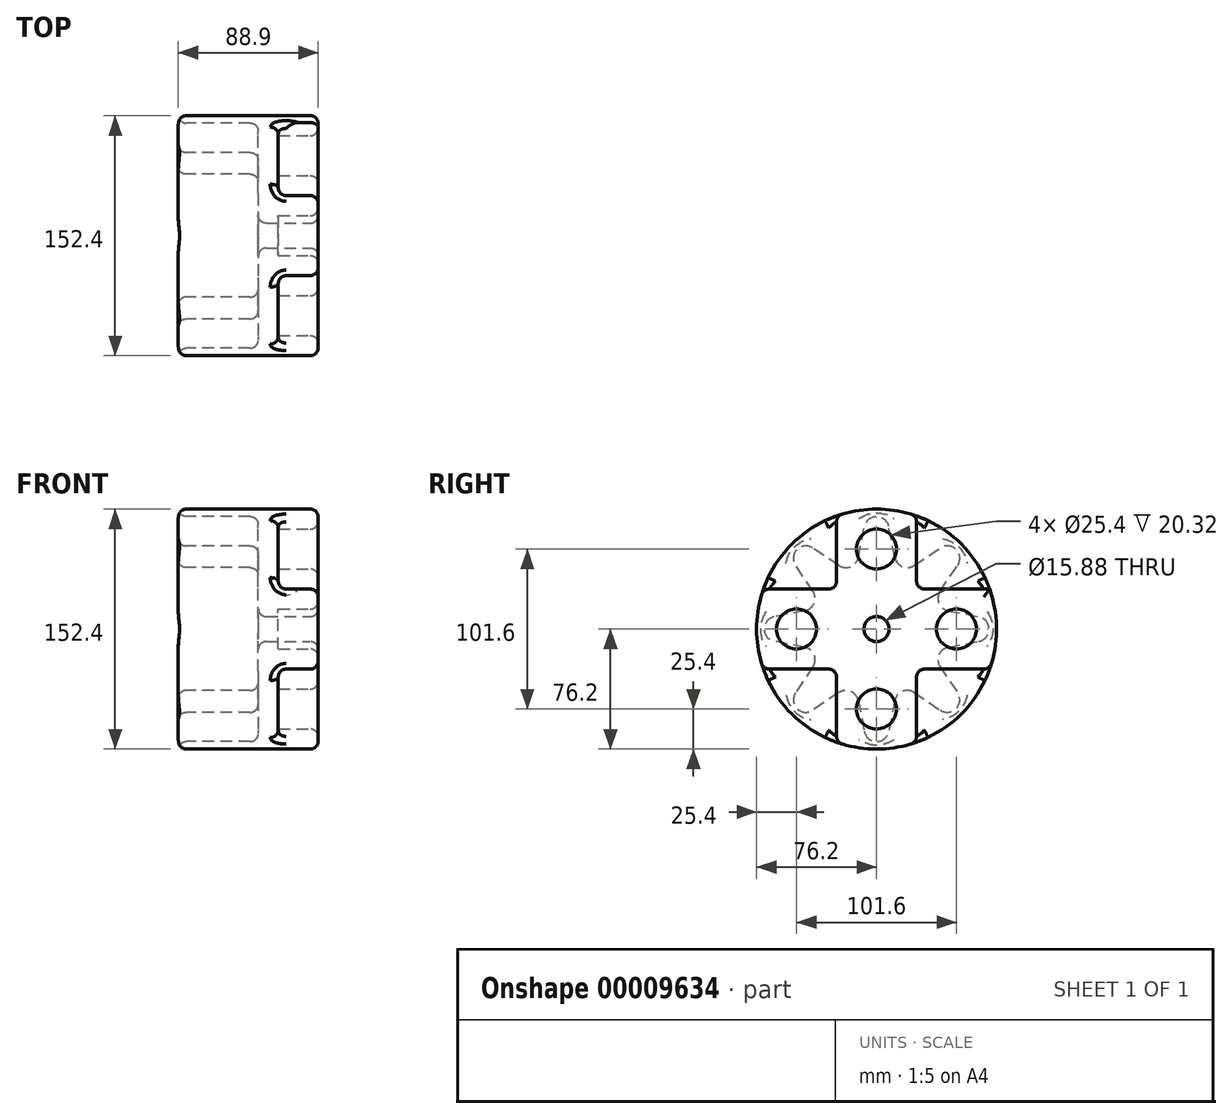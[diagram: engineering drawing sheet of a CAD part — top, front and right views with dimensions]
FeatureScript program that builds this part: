
annotation { "Feature Type Name" : "Feature", "Feature Type Description" : "" }
export const myFeature = defineFeature(function(context is Context, id is Id, definition is map)
    precondition{}
    {
        {
            var Q0;
            Q0=qCreatedBy(makeId("Right.planeOp"),FACE);
            var sketch = newSketch(context, id + "F0", { "sketchPlane" : qUnion([Q0])});
            skCircle(sketch, "E0", {"center": v(0, 0) * mm, "radius": 76.2 * mm});
            skSolve(sketch);
        }
        {
            var Q0;
            Q0 = qSketchRegion(id + "F0", true);
            extrude(context, id + "F1", {"entities" : qUnion([Q0]), "depth" : 88.9 * mm});
        }
        {
            var Q0;
            Q0=makeQuery(id+"F1.opExtrude","CAP_FACE",FACE,{"disambiguationData":[OSD([sQuery(id+"F0.wireOp",EDGE,"E0")])],"isStart":true});
            var sketch = newSketch(context, id + "F2", { "sketchPlane" : qUnion([Q0])});
            skArc(sketch, "E1", {"start": v(7.79, 65.03) * mm, "mid": v(0, 71.44) * mm, "end": v(-7.79, 65.03) * mm});
            skArc(sketch, "E2", {"start": v(-16.4, 39.6) * mm, "mid": v(-13.3, 41.9) * mm, "end": v(-11.65, 45.4) * mm});
            skLineSegment(sketch, "E3", {"start": v(-19.44, 46.93) * mm, "end": v(0, 0) * mm, "construction": true});
            skLineSegment(sketch, "E4", {"start": v(0, 0) * mm, "end": v(0, 63.5) * mm, "construction": true});
            skLineSegment(sketch, "E5", {"start": v(-11.65, 45.4) * mm, "end": v(-7.79, 65.03) * mm});
            skLineSegment(sketch, "E6.0.MirrorCS", {"start": v(11.65, 45.4) * mm, "end": v(7.79, 65.03) * mm});
            skArc(sketch, "E7.0.MirrorCS", {"start": v(-16.4, 39.6) * mm, "mid": v(-20.23, 39.03) * mm, "end": v(-23.86, 40.34) * mm});
            skArc(sketch, "E8.1.0", {"start": v(-39.6, 16.4) * mm, "mid": v(-41.9, 13.3) * mm, "end": v(-45.4, 11.65) * mm});
            skArc(sketch, "E8.1.1", {"start": v(-39.6, 16.4) * mm, "mid": v(-39.03, 20.23) * mm, "end": v(-40.34, 23.86) * mm});
            skLineSegment(sketch, "E8.1.2", {"start": v(-40.34, 23.86) * mm, "end": v(-51.5, 40.48) * mm});
            skArc(sketch, "E8.1.3", {"start": v(-40.48, 51.5) * mm, "mid": v(-50.51, 50.51) * mm, "end": v(-51.5, 40.48) * mm});
            skLineSegment(sketch, "E8.1.4", {"start": v(-23.86, 40.34) * mm, "end": v(-40.48, 51.5) * mm});
            skArc(sketch, "E8.2.0", {"start": v(-39.6, -16.4) * mm, "mid": v(-39.03, -20.23) * mm, "end": v(-40.34, -23.86) * mm});
            skArc(sketch, "E8.2.1", {"start": v(-39.6, -16.4) * mm, "mid": v(-41.9, -13.3) * mm, "end": v(-45.4, -11.65) * mm});
            skLineSegment(sketch, "E8.2.2", {"start": v(-45.4, -11.65) * mm, "end": v(-65.03, -7.79) * mm});
            skArc(sketch, "E8.2.3", {"start": v(-65.03, 7.79) * mm, "mid": v(-71.44, 0) * mm, "end": v(-65.03, -7.79) * mm});
            skLineSegment(sketch, "E8.2.4", {"start": v(-45.4, 11.65) * mm, "end": v(-65.03, 7.79) * mm});
            skArc(sketch, "E8.3.0", {"start": v(-16.4, -39.6) * mm, "mid": v(-13.3, -41.9) * mm, "end": v(-11.65, -45.4) * mm});
            skArc(sketch, "E8.3.1", {"start": v(-16.4, -39.6) * mm, "mid": v(-20.23, -39.03) * mm, "end": v(-23.86, -40.34) * mm});
            skLineSegment(sketch, "E8.3.2", {"start": v(-23.86, -40.34) * mm, "end": v(-40.48, -51.5) * mm});
            skArc(sketch, "E8.3.3", {"start": v(-51.5, -40.48) * mm, "mid": v(-50.51, -50.51) * mm, "end": v(-40.48, -51.5) * mm});
            skLineSegment(sketch, "E8.3.4", {"start": v(-40.34, -23.86) * mm, "end": v(-51.5, -40.48) * mm});
            skArc(sketch, "E8.4.0", {"start": v(16.4, -39.6) * mm, "mid": v(20.23, -39.03) * mm, "end": v(23.86, -40.34) * mm});
            skArc(sketch, "E8.4.1", {"start": v(16.4, -39.6) * mm, "mid": v(13.3, -41.9) * mm, "end": v(11.65, -45.4) * mm});
            skLineSegment(sketch, "E8.4.2", {"start": v(11.65, -45.4) * mm, "end": v(7.79, -65.03) * mm});
            skArc(sketch, "E8.4.3", {"start": v(-7.79, -65.03) * mm, "mid": v(0, -71.44) * mm, "end": v(7.79, -65.03) * mm});
            skLineSegment(sketch, "E8.4.4", {"start": v(-11.65, -45.4) * mm, "end": v(-7.79, -65.03) * mm});
            skArc(sketch, "E8.5.0", {"start": v(39.6, -16.4) * mm, "mid": v(41.9, -13.3) * mm, "end": v(45.4, -11.65) * mm});
            skArc(sketch, "E8.5.1", {"start": v(39.6, -16.4) * mm, "mid": v(39.03, -20.23) * mm, "end": v(40.34, -23.86) * mm});
            skLineSegment(sketch, "E8.5.2", {"start": v(40.34, -23.86) * mm, "end": v(51.5, -40.48) * mm});
            skArc(sketch, "E8.5.3", {"start": v(40.48, -51.5) * mm, "mid": v(50.51, -50.51) * mm, "end": v(51.5, -40.48) * mm});
            skLineSegment(sketch, "E8.5.4", {"start": v(23.86, -40.34) * mm, "end": v(40.48, -51.5) * mm});
            skArc(sketch, "E8.6.0", {"start": v(39.6, 16.4) * mm, "mid": v(39.03, 20.23) * mm, "end": v(40.34, 23.86) * mm});
            skArc(sketch, "E8.6.1", {"start": v(39.6, 16.4) * mm, "mid": v(41.9, 13.3) * mm, "end": v(45.4, 11.65) * mm});
            skLineSegment(sketch, "E8.6.2", {"start": v(45.4, 11.65) * mm, "end": v(65.03, 7.79) * mm});
            skArc(sketch, "E8.6.3", {"start": v(65.03, -7.79) * mm, "mid": v(71.44, 0) * mm, "end": v(65.03, 7.79) * mm});
            skLineSegment(sketch, "E8.6.4", {"start": v(45.4, -11.65) * mm, "end": v(65.03, -7.79) * mm});
            skArc(sketch, "E8.7.0", {"start": v(16.4, 39.6) * mm, "mid": v(13.3, 41.9) * mm, "end": v(11.65, 45.4) * mm});
            skArc(sketch, "E8.7.1", {"start": v(16.4, 39.6) * mm, "mid": v(20.23, 39.03) * mm, "end": v(23.86, 40.34) * mm});
            skLineSegment(sketch, "E8.7.2", {"start": v(23.86, 40.34) * mm, "end": v(40.48, 51.5) * mm});
            skArc(sketch, "E8.7.3", {"start": v(51.5, 40.48) * mm, "mid": v(50.51, 50.51) * mm, "end": v(40.48, 51.5) * mm});
            skLineSegment(sketch, "E8.7.4", {"start": v(40.34, 23.86) * mm, "end": v(51.5, 40.48) * mm});
            skPoint(sketch, "E8.center", {"position": v(0, 0) * mm});
            skSolve(sketch);
        }
        {
            var Q0;
            Q0=makeQuery(id+"F2.imprint","IMPRINT",FACE,{"disambiguationData":[TD([[makeQuery(id+"F2.imprint","IMPRINT",EDGE,{"derivedFrom":sQuery(id+"F2.wireOp",EDGE,"E1")}),1.0]])]});
            var Q1;
            Q1=makeQuery(id+"F1.opExtrude","CAP_FACE",FACE,{"disambiguationData":[OSD([sQuery(id+"F0.wireOp",EDGE,"E0")])],"isStart":false});
            extrude(context, id + "F3", {"entities" : qUnion([Q0]), "operationType" : NewBodyOperationType.REMOVE, "oppositeDirection" : true, "endBoundEntity" : qUnion([Q1]), "depth" : 50.8 * mm});
        }
        {
            var Q0;
            Q0=makeQuery(id+"F1.opExtrude","CAP_FACE",FACE,{"disambiguationData":[OSD([sQuery(id+"F0.wireOp",EDGE,"E0")])],"isStart":false});
            var sketch = newSketch(context, id + "F4", { "sketchPlane" : qUnion([Q0])});
            skCircle(sketch, "E9", {"center": v(0, 50.8) * mm, "radius": 12.7 * mm});
            skCircle(sketch, "E10.1.0", {"center": v(-50.8, 0) * mm, "radius": 12.7 * mm});
            skCircle(sketch, "E10.2.0", {"center": v(0, -50.8) * mm, "radius": 12.7 * mm});
            skCircle(sketch, "E10.3.0", {"center": v(50.8, 0) * mm, "radius": 12.7 * mm});
            skPoint(sketch, "E10.center", {"position": v(0, 0) * mm});
            skLineSegment(sketch, "E11", {"start": v(-50.8, 0) * mm, "end": v(0, 50.8) * mm, "construction": true});
            skLineSegment(sketch, "E12", {"start": v(0, 0) * mm, "end": v(0, 76.2) * mm, "construction": true});
            skLineSegment(sketch, "E13", {"start": v(0, 0) * mm, "end": v(-50.8, 0) * mm, "construction": true});
            skSolve(sketch);
        }
        {
            var Q0;
            Q0 = qSketchRegion(id + "F4", true);
            extrude(context, id + "F5", {"entities" : qUnion([Q0]), "operationType" : NewBodyOperationType.REMOVE, "oppositeDirection" : true, "depth" : 25.4 * mm});
        }
        {
            var Q0;
            Q0=makeQuery(id+"F1.opExtrude","CAP_FACE",FACE,{"disambiguationData":[OSD([sQuery(id+"F0.wireOp",EDGE,"E0")])],"isStart":false});
            var sketch = newSketch(context, id + "F6", { "sketchPlane" : qUnion([Q0])});
            skLineSegment(sketch, "E14.top", {"start": v(-71.84, 25.4) * mm, "end": v(-25.4, 25.4) * mm});
            skLineSegment(sketch, "E14.right", {"start": v(-25.4, 71.84) * mm, "end": v(-25.4, 25.4) * mm});
            skLineSegment(sketch, "E15", {"start": v(0, 63.5) * mm, "end": v(0, 76.2) * mm, "construction": true});
            skLineSegment(sketch, "E16", {"start": v(-12.7, 50.8) * mm, "end": v(-25.4, 50.8) * mm, "construction": true});
            skCircle(sketch, "E17.0", {"center": v(0, 50.8) * mm, "radius": 12.7 * mm, "construction": true});
            skArc(sketch, "E18.0", {"start": v(-25.4, 71.84) * mm, "mid": v(-53.88, 53.88) * mm, "end": v(-71.84, 25.4) * mm});
            skLineSegment(sketch, "E19.1.0", {"start": v(-71.84, -25.4) * mm, "end": v(-25.4, -25.4) * mm});
            skArc(sketch, "E19.1.1", {"start": v(-71.84, -25.4) * mm, "mid": v(-53.88, -53.88) * mm, "end": v(-25.4, -71.84) * mm});
            skLineSegment(sketch, "E19.1.2", {"start": v(-25.4, -71.84) * mm, "end": v(-25.4, -25.4) * mm});
            skLineSegment(sketch, "E19.2.0", {"start": v(25.4, -71.84) * mm, "end": v(25.4, -25.4) * mm});
            skArc(sketch, "E19.2.1", {"start": v(25.4, -71.84) * mm, "mid": v(53.88, -53.88) * mm, "end": v(71.84, -25.4) * mm});
            skLineSegment(sketch, "E19.2.2", {"start": v(71.84, -25.4) * mm, "end": v(25.4, -25.4) * mm});
            skLineSegment(sketch, "E19.3.0", {"start": v(71.84, 25.4) * mm, "end": v(25.4, 25.4) * mm});
            skArc(sketch, "E19.3.1", {"start": v(71.84, 25.4) * mm, "mid": v(53.88, 53.88) * mm, "end": v(25.4, 71.84) * mm});
            skLineSegment(sketch, "E19.3.2", {"start": v(25.4, 71.84) * mm, "end": v(25.4, 25.4) * mm});
            skSolve(sketch);
        }
        {
            var Q0;
            Q0 = qSketchRegion(id + "F6", true);
            extrude(context, id + "F7", {"entities" : qUnion([Q0]), "operationType" : NewBodyOperationType.REMOVE, "oppositeDirection" : true, "depth" : 25.4 * mm});
        }
        {
            var Q0;
            {var subQ10=sQuery(id+"F6.wireOp",EDGE,"E14.top");Q0=makeQuery(id+"F6.imprint","IMPRINT",FACE,{"disambiguationData":[TD([[makeQuery(id+"F6.imprint","IMPRINT",EDGE,{"derivedFrom":subQ10}),-1.0]])]});}
            var sketch = newSketch(context, id + "F8", { "sketchPlane" : qUnion([Q0])});
            skCircle(sketch, "E20", {"center": v(0, 0) * mm, "radius": 7.94 * mm});
            skSolve(sketch);
        }
        {
            var Q0;
            Q0 = qSketchRegion(id + "F8", true);
            var Q1;
            Q1=makeQuery(id+"F3.boolean.opBoolean","COPY",FACE,{"derivedFrom":makeQuery(id+"F3.opExtrude","CAP_FACE",FACE,{"disambiguationData":[OSD([sQuery(id+"F2.wireOp",EDGE,"E1"),sQuery(id+"F2.wireOp",EDGE,"E2"),sQuery(id+"F2.wireOp",EDGE,"E5"),sQuery(id+"F2.wireOp",EDGE,"E6.0.MirrorCS"),sQuery(id+"F2.wireOp",EDGE,"E7.0.MirrorCS"),sQuery(id+"F2.wireOp",EDGE,"E8.1.0"),sQuery(id+"F2.wireOp",EDGE,"E8.1.1"),sQuery(id+"F2.wireOp",EDGE,"E8.1.2"),sQuery(id+"F2.wireOp",EDGE,"E8.1.3"),sQuery(id+"F2.wireOp",EDGE,"E8.1.4"),sQuery(id+"F2.wireOp",EDGE,"E8.2.0"),sQuery(id+"F2.wireOp",EDGE,"E8.2.1"),sQuery(id+"F2.wireOp",EDGE,"E8.2.2"),sQuery(id+"F2.wireOp",EDGE,"E8.2.3"),sQuery(id+"F2.wireOp",EDGE,"E8.2.4"),sQuery(id+"F2.wireOp",EDGE,"E8.3.0"),sQuery(id+"F2.wireOp",EDGE,"E8.3.1"),sQuery(id+"F2.wireOp",EDGE,"E8.3.2"),sQuery(id+"F2.wireOp",EDGE,"E8.3.3"),sQuery(id+"F2.wireOp",EDGE,"E8.3.4"),sQuery(id+"F2.wireOp",EDGE,"E8.4.0"),sQuery(id+"F2.wireOp",EDGE,"E8.4.1"),sQuery(id+"F2.wireOp",EDGE,"E8.4.2"),sQuery(id+"F2.wireOp",EDGE,"E8.4.3"),sQuery(id+"F2.wireOp",EDGE,"E8.4.4"),sQuery(id+"F2.wireOp",EDGE,"E8.5.0"),sQuery(id+"F2.wireOp",EDGE,"E8.5.1"),sQuery(id+"F2.wireOp",EDGE,"E8.5.2"),sQuery(id+"F2.wireOp",EDGE,"E8.5.3"),sQuery(id+"F2.wireOp",EDGE,"E8.5.4"),sQuery(id+"F2.wireOp",EDGE,"E8.6.0"),sQuery(id+"F2.wireOp",EDGE,"E8.6.1"),sQuery(id+"F2.wireOp",EDGE,"E8.6.2"),sQuery(id+"F2.wireOp",EDGE,"E8.6.3"),sQuery(id+"F2.wireOp",EDGE,"E8.6.4"),sQuery(id+"F2.wireOp",EDGE,"E8.7.0"),sQuery(id+"F2.wireOp",EDGE,"E8.7.1"),sQuery(id+"F2.wireOp",EDGE,"E8.7.2"),sQuery(id+"F2.wireOp",EDGE,"E8.7.3"),sQuery(id+"F2.wireOp",EDGE,"E8.7.4")])],"isStart":false})});
            extrude(context, id + "F9", {"entities" : qUnion([Q0]), "operationType" : NewBodyOperationType.REMOVE, "endBound" : BoundingType.UP_TO_SURFACE, "oppositeDirection" : true, "endBoundEntityFace" : qUnion([Q1]), "depth" : 25.4 * mm});
        }
        {
            var Q0;
            Q0=makeQuery(id+"F3.boolean.opBoolean","COPY",FACE,{"derivedFrom":makeQuery(id+"F3.opExtrude","CAP_FACE",FACE,{"disambiguationData":[OSD([sQuery(id+"F2.wireOp",EDGE,"E1"),sQuery(id+"F2.wireOp",EDGE,"E2"),sQuery(id+"F2.wireOp",EDGE,"E5"),sQuery(id+"F2.wireOp",EDGE,"E6.0.MirrorCS"),sQuery(id+"F2.wireOp",EDGE,"E7.0.MirrorCS"),sQuery(id+"F2.wireOp",EDGE,"E8.1.0"),sQuery(id+"F2.wireOp",EDGE,"E8.1.1"),sQuery(id+"F2.wireOp",EDGE,"E8.1.2"),sQuery(id+"F2.wireOp",EDGE,"E8.1.3"),sQuery(id+"F2.wireOp",EDGE,"E8.1.4"),sQuery(id+"F2.wireOp",EDGE,"E8.2.0"),sQuery(id+"F2.wireOp",EDGE,"E8.2.1"),sQuery(id+"F2.wireOp",EDGE,"E8.2.2"),sQuery(id+"F2.wireOp",EDGE,"E8.2.3"),sQuery(id+"F2.wireOp",EDGE,"E8.2.4"),sQuery(id+"F2.wireOp",EDGE,"E8.3.0"),sQuery(id+"F2.wireOp",EDGE,"E8.3.1"),sQuery(id+"F2.wireOp",EDGE,"E8.3.2"),sQuery(id+"F2.wireOp",EDGE,"E8.3.3"),sQuery(id+"F2.wireOp",EDGE,"E8.3.4"),sQuery(id+"F2.wireOp",EDGE,"E8.4.0"),sQuery(id+"F2.wireOp",EDGE,"E8.4.1"),sQuery(id+"F2.wireOp",EDGE,"E8.4.2"),sQuery(id+"F2.wireOp",EDGE,"E8.4.3"),sQuery(id+"F2.wireOp",EDGE,"E8.4.4"),sQuery(id+"F2.wireOp",EDGE,"E8.5.0"),sQuery(id+"F2.wireOp",EDGE,"E8.5.1"),sQuery(id+"F2.wireOp",EDGE,"E8.5.2"),sQuery(id+"F2.wireOp",EDGE,"E8.5.3"),sQuery(id+"F2.wireOp",EDGE,"E8.5.4"),sQuery(id+"F2.wireOp",EDGE,"E8.6.0"),sQuery(id+"F2.wireOp",EDGE,"E8.6.1"),sQuery(id+"F2.wireOp",EDGE,"E8.6.2"),sQuery(id+"F2.wireOp",EDGE,"E8.6.3"),sQuery(id+"F2.wireOp",EDGE,"E8.6.4"),sQuery(id+"F2.wireOp",EDGE,"E8.7.0"),sQuery(id+"F2.wireOp",EDGE,"E8.7.1"),sQuery(id+"F2.wireOp",EDGE,"E8.7.2"),sQuery(id+"F2.wireOp",EDGE,"E8.7.3"),sQuery(id+"F2.wireOp",EDGE,"E8.7.4")])],"isStart":false})});
            var Q1;
            Q1=makeQuery(id+"F1.opExtrude","CAP_FACE",FACE,{"disambiguationData":[OSD([sQuery(id+"F0.wireOp",EDGE,"E0")])],"isStart":true});
            fillet(context, id + "F10", {"entities" : qUnion([Q0, Q1]), "radius" : 5.08 * mm, "tangentPropagation" : true, "allowEdgeOverflow" : false});
        }
        {
            var Q0;
            Q0=makeQuery(id+"F7.boolean.opBoolean","COPY",FACE,{"derivedFrom":makeQuery(id+"F7.opExtrude","SWEPT_FACE",FACE,{"disambiguationData":[OSD([sQuery(id+"F6.wireOp",EDGE,"E14.top")])]})});
            var Q1;
            Q1=makeQuery(id+"F7.boolean.opBoolean","COPY",FACE,{"derivedFrom":makeQuery(id+"F7.opExtrude","CAP_FACE",FACE,{"disambiguationData":[OSD([sQuery(id+"F6.wireOp",EDGE,"E14.top"),sQuery(id+"F6.wireOp",EDGE,"E14.right"),sQuery(id+"F6.wireOp",EDGE,"E18.0")])],"isStart":false})});
            var Q2;
            Q2=makeQuery(id+"F7.boolean.opBoolean","COPY",FACE,{"derivedFrom":makeQuery(id+"F7.opExtrude","SWEPT_FACE",FACE,{"disambiguationData":[OSD([sQuery(id+"F6.wireOp",EDGE,"E14.right")])]})});
            var Q3;
            Q3=makeQuery(id+"F7.boolean.opBoolean","COPY",FACE,{"derivedFrom":makeQuery(id+"F7.opExtrude","CAP_FACE",FACE,{"disambiguationData":[OSD([sQuery(id+"F6.wireOp",EDGE,"E19.3.0"),sQuery(id+"F6.wireOp",EDGE,"E19.3.1"),sQuery(id+"F6.wireOp",EDGE,"E19.3.2")])],"isStart":false})});
            var Q4;
            Q4=makeQuery(id+"F7.boolean.opBoolean","COPY",FACE,{"derivedFrom":makeQuery(id+"F7.opExtrude","CAP_FACE",FACE,{"disambiguationData":[OSD([sQuery(id+"F6.wireOp",EDGE,"E19.2.0"),sQuery(id+"F6.wireOp",EDGE,"E19.2.1"),sQuery(id+"F6.wireOp",EDGE,"E19.2.2")])],"isStart":false})});
            var Q5;
            Q5=makeQuery(id+"F7.boolean.opBoolean","COPY",FACE,{"derivedFrom":makeQuery(id+"F7.opExtrude","CAP_FACE",FACE,{"disambiguationData":[OSD([sQuery(id+"F6.wireOp",EDGE,"E19.1.0"),sQuery(id+"F6.wireOp",EDGE,"E19.1.1"),sQuery(id+"F6.wireOp",EDGE,"E19.1.2")])],"isStart":false})});
            var Q6;
            Q6=makeQuery(id+"F7.boolean.opBoolean","COPY",FACE,{"derivedFrom":makeQuery(id+"F7.opExtrude","SWEPT_FACE",FACE,{"disambiguationData":[OSD([sQuery(id+"F6.wireOp",EDGE,"E19.3.2")])]})});
            var Q7;
            Q7=makeQuery(id+"F7.boolean.opBoolean","COPY",FACE,{"derivedFrom":makeQuery(id+"F7.opExtrude","SWEPT_FACE",FACE,{"disambiguationData":[OSD([sQuery(id+"F6.wireOp",EDGE,"E19.2.0")])]})});
            var Q8;
            Q8=makeQuery(id+"F7.boolean.opBoolean","COPY",FACE,{"derivedFrom":makeQuery(id+"F7.opExtrude","SWEPT_FACE",FACE,{"disambiguationData":[OSD([sQuery(id+"F6.wireOp",EDGE,"E19.1.2")])]})});
            var Q9;
            Q9=makeQuery(id+"F7.boolean.opBoolean","COPY",FACE,{"derivedFrom":makeQuery(id+"F7.opExtrude","SWEPT_FACE",FACE,{"disambiguationData":[OSD([sQuery(id+"F6.wireOp",EDGE,"E19.1.0")])]})});
            var Q10;
            Q10=makeQuery(id+"F7.boolean.opBoolean","COPY",FACE,{"derivedFrom":makeQuery(id+"F7.opExtrude","SWEPT_FACE",FACE,{"disambiguationData":[OSD([sQuery(id+"F6.wireOp",EDGE,"E19.2.2")])]})});
            var Q11;
            Q11=makeQuery(id+"F1.opExtrude","CAP_FACE",FACE,{"disambiguationData":[OSD([sQuery(id+"F0.wireOp",EDGE,"E0")])],"isStart":false});
            fillet(context, id + "F11", {"entities" : qUnion([Q0, Q1, Q2, Q3, Q4, Q5, Q6, Q7, Q8, Q9, Q10, Q11]), "radius" : 5.08 * mm, "tangentPropagation" : true, "allowEdgeOverflow" : false});
        }
    });
